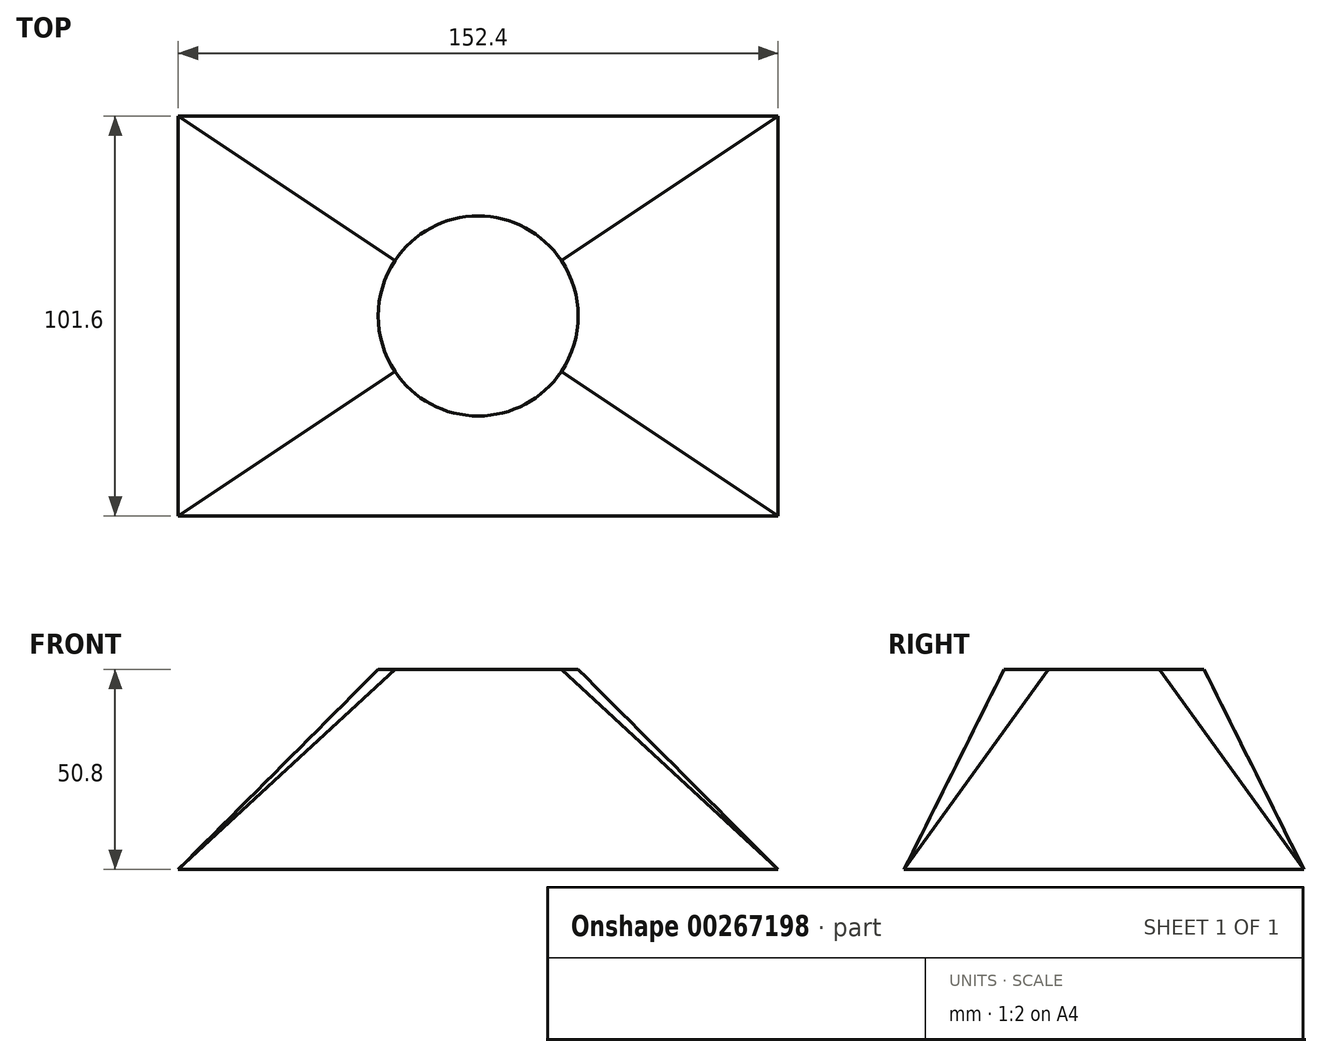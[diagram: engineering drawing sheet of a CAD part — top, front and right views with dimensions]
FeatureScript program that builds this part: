
annotation { "Feature Type Name" : "Feature", "Feature Type Description" : "" }
export const myFeature = defineFeature(function(context is Context, id is Id, definition is map)
    precondition{}
    {
        {
            var Q0;
            Q0=qCreatedBy(makeId("Top.planeOp"),FACE);
            var sketch = newSketch(context, id + "F0", { "sketchPlane" : qUnion([Q0])});
            skLineSegment(sketch, "E0.bottom", {"start": v(76.2, -50.8) * mm, "end": v(-76.2, -50.8) * mm});
            skLineSegment(sketch, "E0.top", {"start": v(76.2, 50.8) * mm, "end": v(-76.2, 50.8) * mm});
            skLineSegment(sketch, "E0.left", {"start": v(76.2, -50.8) * mm, "end": v(76.2, 50.8) * mm});
            skLineSegment(sketch, "E0.right", {"start": v(-76.2, -50.8) * mm, "end": v(-76.2, 50.8) * mm});
            skPoint(sketch, "E0.middle", {"position": v(0, 0) * mm});
            skSolve(sketch);
        }
        {
            var Q0;
            Q0=qCreatedBy(makeId("Top.planeOp"),FACE);
            cPlane(context, id + "F1", {"entities" : qUnion([Q0]), "cplaneType" : CPlaneType.OFFSET, "offset" : 50.8 * mm, "width" : 152.4 * mm, "height" : 152.4 * mm});
        }
        {
            var Q0;
            Q0=qCreatedBy(id+"F1.planeOp",FACE);
            var sketch = newSketch(context, id + "F2", { "sketchPlane" : qUnion([Q0])});
            skPoint(sketch, "E1.0", {"position": v(-76.2, 50.8) * mm});
            skPoint(sketch, "E1.1", {"position": v(76.2, 50.8) * mm});
            skPoint(sketch, "E1.2", {"position": v(76.2, -50.8) * mm});
            skPoint(sketch, "E1.3", {"position": v(-76.2, -50.8) * mm});
            skLineSegment(sketch, "E2", {"start": v(-76.2, 50.8) * mm, "end": v(0, 0) * mm, "construction": true});
            skLineSegment(sketch, "E3", {"start": v(76.2, 50.8) * mm, "end": v(0, 0) * mm, "construction": true});
            skLineSegment(sketch, "E4", {"start": v(76.2, -50.8) * mm, "end": v(0, 0) * mm, "construction": true});
            skLineSegment(sketch, "E5", {"start": v(-76.2, -50.8) * mm, "end": v(0, 0) * mm, "construction": true});
            skArc(sketch, "E6", {"start": v(-21.13, 14.09) * mm, "mid": v(-25.4, 0) * mm, "end": v(-21.13, -14.09) * mm});
            skLineSegment(sketch, "E7", {"start": v(21.13, 14.09) * mm, "end": v(21.13, 14.09) * mm});
            skLineSegment(sketch, "E8", {"start": v(21.13, -14.09) * mm, "end": v(21.13, -14.09) * mm});
            skArc(sketch, "E9", {"start": v(21.13, 14.09) * mm, "mid": v(0, 25.4) * mm, "end": v(-21.13, 14.09) * mm});
            skArc(sketch, "E10", {"start": v(21.13, -14.09) * mm, "mid": v(25.4, 0) * mm, "end": v(21.13, 14.09) * mm});
            skArc(sketch, "E11", {"start": v(-21.13, -14.09) * mm, "mid": v(0, -25.4) * mm, "end": v(21.13, -14.09) * mm});
            skSolve(sketch);
        }
        {
            var Q0;
            Q0=makeQuery(id+"F0.imprint","IMPRINT",FACE,{"disambiguationData":[TD([[makeQuery(id+"F0.imprint","IMPRINT",EDGE,{"derivedFrom":sQuery(id+"F0.wireOp",EDGE,"E0.bottom")}),-1.0]])]});
            var Q1;
            Q1=makeQuery(id+"F2.imprint","IMPRINT",FACE,{"disambiguationData":[TD([[makeQuery(id+"F2.imprint","IMPRINT",EDGE,{"derivedFrom":sQuery(id+"F2.wireOp",EDGE,"E6")}),1.0]])]});
            loft(context, id + "F3", {"sheetProfilesArray" : [{ "sheetProfileEntities" : qUnion([Q0]) }, { "sheetProfileEntities" : qUnion([Q1]) }]});
        }
    });
